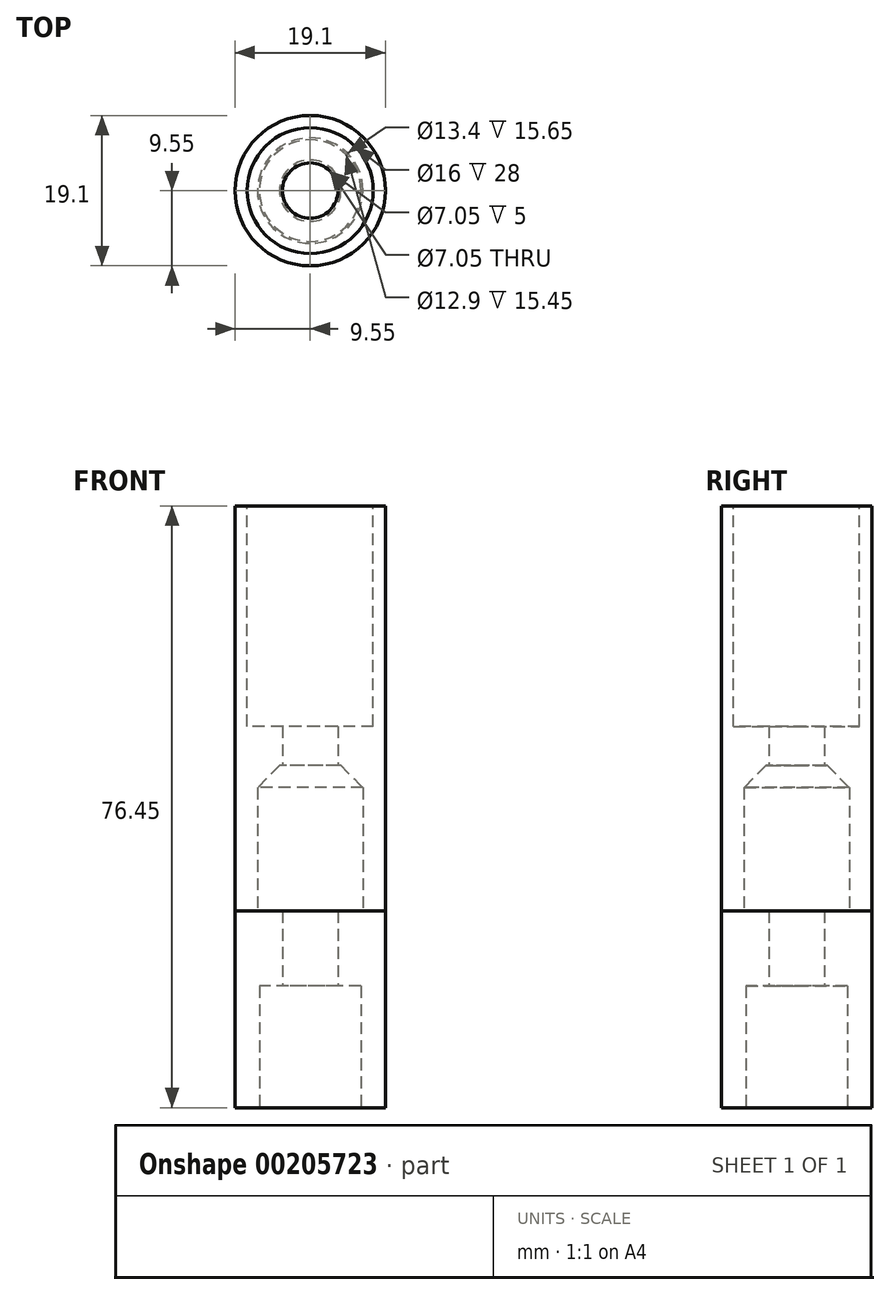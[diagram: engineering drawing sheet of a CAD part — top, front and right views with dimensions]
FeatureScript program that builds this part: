
annotation { "Feature Type Name" : "Feature", "Feature Type Description" : "" }
export const myFeature = defineFeature(function(context is Context, id is Id, definition is map)
    precondition{}
    {
        {
            assignVariable(context, id + "F0", {"name" : "stemMaleHeight", "anyValue" : 15.4});
        }
        {
            assignVariable(context, id + "F1", {"name" : "stemHeight", "anyValue" : 25});
        }
        {
            assignVariable(context, id + "F2", {"name" : "stemFemaleHeight", "anyValue" : 15.45});
        }
        {
            var Q0;
            Q0=qCreatedBy(makeId("Top.planeOp"),FACE);
            var sketch = newSketch(context, id + "F3", { "sketchPlane" : qUnion([Q0])});
            skCircle(sketch, "E0", {"center": v(0, 0) * mm, "radius": 3.52 * mm});
            skCircle(sketch, "E1", {"center": v(0, 0) * mm, "radius": 6.45 * mm});
            skCircle(sketch, "E2", {"center": v(0, 0) * mm, "radius": 9.55 * mm});
            skSolve(sketch);
        }
        {
            var Q0;
            Q0=makeQuery(id+"F3.imprint","IMPRINT",FACE,{"disambiguationData":[TD([[makeQuery(id+"F3.imprint","IMPRINT",EDGE,{"derivedFrom":sQuery(id+"F3.wireOp",EDGE,"E1")}),-1.0]])]});
            var Q1;
            Q1=makeQuery(id+"F3.imprint","IMPRINT",FACE,{"disambiguationData":[TD([[makeQuery(id+"F3.imprint","IMPRINT",EDGE,{"derivedFrom":sQuery(id+"F3.wireOp",EDGE,"E0")}),-1.0]])]});
            var Q2;
            Q2=makeQuery(id+"F3.imprint","IMPRINT",FACE,{"disambiguationData":[TD([[makeQuery(id+"F3.imprint","IMPRINT",EDGE,{"derivedFrom":sQuery(id+"F3.wireOp",EDGE,"E0")}),1.0]])]});
            extrude(context, id + "F4", {"entities" : qUnion([Q0, Q1, Q2]), "depth" : (getVariable(context, 'stemHeight')) * mm});
        }
        {
            var Q0;
            Q0=makeQuery(id+"F3.imprint","IMPRINT",FACE,{"disambiguationData":[TD([[makeQuery(id+"F3.imprint","IMPRINT",EDGE,{"derivedFrom":sQuery(id+"F3.wireOp",EDGE,"E0")}),-1.0]])]});
            var Q1;
            Q1=makeQuery(id+"F3.imprint","IMPRINT",FACE,{"disambiguationData":[TD([[makeQuery(id+"F3.imprint","IMPRINT",EDGE,{"derivedFrom":sQuery(id+"F3.wireOp",EDGE,"E0")}),1.0]])]});
            extrude(context, id + "F5", {"entities" : qUnion([Q0, Q1]), "operationType" : NewBodyOperationType.ADD, "depth" : (getVariable(context, 'stemHeight') + getVariable(context, 'stemMaleHeight')) * mm});
        }
        {
            var Q0;
            Q0=makeQuery(id+"F3.imprint","IMPRINT",FACE,{"disambiguationData":[TD([[makeQuery(id+"F3.imprint","IMPRINT",EDGE,{"derivedFrom":sQuery(id+"F3.wireOp",EDGE,"E0")}),1.0]])]});
            extrude(context, id + "F6", {"entities" : qUnion([Q0]), "operationType" : NewBodyOperationType.REMOVE, "endBound" : BoundingType.THROUGH_ALL, "depth" : 25 * mm});
        }
        {
            var Q0;
            Q0=makeQuery(id+"F3.imprint","IMPRINT",FACE,{"disambiguationData":[TD([[makeQuery(id+"F3.imprint","IMPRINT",EDGE,{"derivedFrom":sQuery(id+"F3.wireOp",EDGE,"E0")}),-1.0]])]});
            extrude(context, id + "F7", {"entities" : qUnion([Q0]), "operationType" : NewBodyOperationType.REMOVE, "depth" : (getVariable(context, 'stemFemaleHeight')) * mm});
        }
        {
            assignVariable(context, id + "F8", {"name" : "neckHoleHeight", "anyValue" : 28});
        }
        {
            assignVariable(context, id + "F9", {"name" : "neckShelfHeight", "anyValue" : 8});
        }
        {
            var Q0;
            Q0=makeQuery(id+"F4.opExtrude","CAP_FACE",FACE,{"disambiguationData":[OSD([sQuery(id+"F3.wireOp",EDGE,"E2")])],"isStart":false});
            var sketch = newSketch(context, id + "F10", { "sketchPlane" : qUnion([Q0])});
            skCircle(sketch, "E3.0", {"center": v(0, 0) * mm, "radius": 6.7 * mm});
            skCircle(sketch, "E4.0", {"center": v(0, 0) * mm, "radius": 9.55 * mm});
            skSolve(sketch);
        }
        {
            var Q0;
            Q0 = qSketchRegion(id + "F10", true);
            var Q1;
            Q1=makeQuery(id+"F10.imprint","IMPRINT",FACE,{"disambiguationData":[TD([[makeQuery(id+"F10.imprint","IMPRINT",EDGE,{"derivedFrom":makeQuery(id+"F5.boolean.opBoolean","INTERSECT",EDGE,{"derivedFrom":[makeQuery(id+"F4.opExtrude","CAP_FACE",FACE,{"disambiguationData":[OSD([sQuery(id+"F3.wireOp",EDGE,"E2")])],"isStart":false}),makeQuery(id+"F5.opExtrude","SWEPT_FACE",FACE,{"disambiguationData":[OSD([sQuery(id+"F3.wireOp",EDGE,"E1")])]})]})}),-1.0]])]});
            var Q2;
            Q2=makeQuery(id+"F10.imprint","IMPRINT",FACE,{"disambiguationData":[TD([[makeQuery(id+"F10.imprint","IMPRINT",EDGE,{"derivedFrom":sQuery(id+"F10.wireOp",EDGE,"E3.0")}),1.0]])]});
            extrude(context, id + "F11", {"entities" : qUnion([Q0, Q1, Q2]), "depth" : (getVariable(context, 'stemFemaleHeight') + getVariable(context, 'neckHoleHeight') + getVariable(context, 'neckShelfHeight')) * mm});
        }
        {
            var Q0;
            Q0=makeQuery(id+"F10.imprint","IMPRINT",FACE,{"disambiguationData":[TD([[makeQuery(id+"F10.imprint","IMPRINT",EDGE,{"derivedFrom":sQuery(id+"F10.wireOp",EDGE,"E3.0")}),1.0]])]});
            var Q1;
            Q1=makeQuery(id+"F10.imprint","IMPRINT",FACE,{"disambiguationData":[TD([[makeQuery(id+"F10.imprint","IMPRINT",EDGE,{"derivedFrom":makeQuery(id+"F5.boolean.opBoolean","INTERSECT",EDGE,{"derivedFrom":[makeQuery(id+"F4.opExtrude","CAP_FACE",FACE,{"disambiguationData":[OSD([sQuery(id+"F3.wireOp",EDGE,"E2")])],"isStart":false}),makeQuery(id+"F5.opExtrude","SWEPT_FACE",FACE,{"disambiguationData":[OSD([sQuery(id+"F3.wireOp",EDGE,"E1")])]})]})}),-1.0]])]});
            extrude(context, id + "F12", {"entities" : qUnion([Q0, Q1]), "operationType" : NewBodyOperationType.REMOVE, "depth" : (getVariable(context, 'stemFemaleHeight') + getVariable(context, 'neckShelfHeight') - 5) * mm});
        }
        {
            var Q0;
            Q0=makeQuery(id+"F11.opExtrude","CAP_FACE",FACE,{"disambiguationData":[OSD([sQuery(id+"F10.wireOp",EDGE,"E4.0")])],"isStart":false});
            var sketch = newSketch(context, id + "F13", { "sketchPlane" : qUnion([Q0])});
            skCircle(sketch, "E5", {"center": v(0, 0) * mm, "radius": 8 * mm});
            skSolve(sketch);
        }
        {
            var Q0;
            Q0=makeQuery(id+"F13.imprint","IMPRINT",FACE,{"disambiguationData":[TD([[makeQuery(id+"F13.imprint","IMPRINT",EDGE,{"derivedFrom":sQuery(id+"F13.wireOp",EDGE,"E5")}),1.0]])]});
            extrude(context, id + "F14", {"entities" : qUnion([Q0]), "operationType" : NewBodyOperationType.REMOVE, "oppositeDirection" : true, "depth" : (getVariable(context, 'neckHoleHeight')) * mm});
        }
        {
            var Q0;
            Q0=makeQuery(id+"F12.boolean.opBoolean","COPY",EDGE,{"derivedFrom":makeQuery(id+"F12.opExtrude","CAP_EDGE",EDGE,{"disambiguationData":[OSD([sQuery(id+"F10.wireOp",EDGE,"E3.0")])],"isStart":false})});
            chamfer(context, id + "F15", {"entities" : qUnion([Q0]), "chamferType" : ChamferType.OFFSET_ANGLE, "width" : 2.8 * mm, "oppositeDirection" : false, "angle" : 45 * degree, "tangentPropagation" : true});
        }
        {
            var Q0;
            Q0=makeQuery(id+"F3.imprint","IMPRINT",FACE,{"disambiguationData":[TD([[makeQuery(id+"F3.imprint","IMPRINT",EDGE,{"derivedFrom":sQuery(id+"F3.wireOp",EDGE,"E0")}),1.0]])]});
            var Q1;
            Q1=sQuery(id+"F3.wireOp",EDGE,"E0");
            extrude(context, id + "F16", {"entities" : qUnion([Q0]), "operationType" : NewBodyOperationType.REMOVE, "surfaceEntities" : qUnion([Q1]), "endBound" : BoundingType.THROUGH_ALL, "depth" : 25 * mm});
        }
    });
